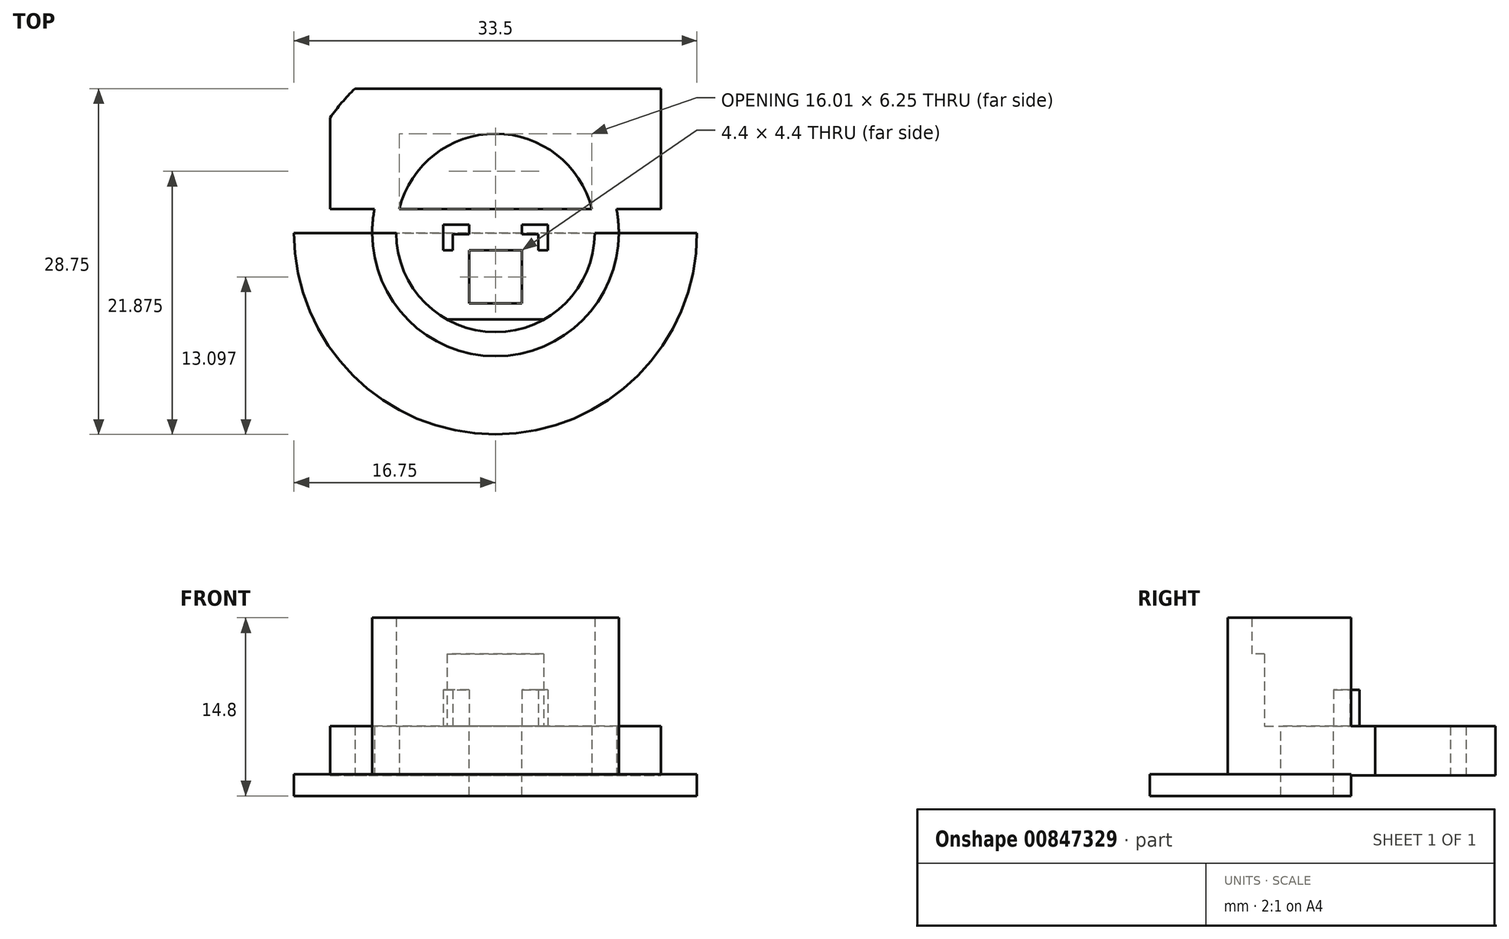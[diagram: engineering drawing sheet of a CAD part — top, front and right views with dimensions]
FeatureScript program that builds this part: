
annotation { "Feature Type Name" : "Feature", "Feature Type Description" : "" }
export const myFeature = defineFeature(function(context is Context, id is Id, definition is map)
    precondition{}
    {
        {
            var Q0;
            Q0=qCreatedBy(makeId("Top.planeOp"),FACE);
            var sketch = newSketch(context, id + "F0", { "sketchPlane" : qUnion([Q0])});
            skCircle(sketch, "E0", {"center": v(0, 0) * mm, "radius": 16.75 * mm});
            skCircle(sketch, "E1", {"center": v(0, 0) * mm, "radius": 10.25 * mm});
            skPoint(sketch, "E2", {"position": v(-16.75, 0) * mm});
            skPoint(sketch, "E3", {"position": v(16.75, 0) * mm});
            skPoint(sketch, "E4", {"position": v(10.25, 0) * mm});
            skPoint(sketch, "E5", {"position": v(-10.25, 0) * mm});
            skLineSegment(sketch, "E6", {"start": v(-16.75, 0) * mm, "end": v(-16.75, 12) * mm});
            skLineSegment(sketch, "E7", {"start": v(-16.75, 12) * mm, "end": v(16.75, 12) * mm});
            skLineSegment(sketch, "E8", {"start": v(16.75, 12) * mm, "end": v(16.75, 0) * mm});
            skLineSegment(sketch, "E9", {"start": v(-16.75, 0) * mm, "end": v(-10.25, 0) * mm});
            skLineSegment(sketch, "E10", {"start": v(10.25, 0) * mm, "end": v(16.75, 0) * mm});
            skLineSegment(sketch, "E11", {"start": v(-10.25, 0) * mm, "end": v(10.25, 0) * mm});
            skLineSegment(sketch, "E12", {"start": v(-13.75, 12) * mm, "end": v(-13.75, 0) * mm});
            skLineSegment(sketch, "E13", {"start": v(13.75, 12) * mm, "end": v(13.75, 0) * mm});
            skCircle(sketch, "E14", {"center": v(0, 0) * mm, "radius": 8.25 * mm});
            skLineSegment(sketch, "E15", {"start": v(-13.75, 2) * mm, "end": v(13.75, 2) * mm});
            skSolve(sketch);
        }
        {
            var Q0;
            {var subQ0=sQuery(id+"F0.wireOp",EDGE,"E9");Q0=makeQuery(id+"F0.imprint","IMPRINT",FACE,{"disambiguationData":[TD([[makeQuery(id+"F0.imprint","IMPRINT",EDGE,{"derivedFrom":subQ0}),-1.0]])]});}
            var Q1;
            {var subQ0=sQuery(id+"F0.wireOp",EDGE,"E11");var subQ4=sQuery(id+"F0.wireOp",EDGE,"E14");var subQ5=makeQuery(id+"F0.imprint","INTERSECT",VERTEX,{"disambiguationData":[OD(0.0)],"derivedFrom":[subQ0,subQ4]});Q1=makeQuery(id+"F0.imprint","IMPRINT",FACE,{"disambiguationData":[TD([[makeQuery(id+"F0.imprint","IMPRINT",EDGE,{"disambiguationData":[TD([[subQ5,-1.0]])],"derivedFrom":subQ4}),-1.0]])]});}
            var Q2;
            {var subQ0=sQuery(id+"F0.wireOp",EDGE,"E14");var subQ1=sQuery(id+"F0.wireOp",EDGE,"E11");var subQ2=makeQuery(id+"F0.imprint","INTERSECT",VERTEX,{"disambiguationData":[OD(0.0)],"derivedFrom":[subQ1,subQ0]});Q2=makeQuery(id+"F0.imprint","IMPRINT",FACE,{"disambiguationData":[TD([[makeQuery(id+"F0.imprint","IMPRINT",EDGE,{"disambiguationData":[TD([[subQ2,-1.0]])],"derivedFrom":subQ1}),-1.0]])]});}
            var Q3;
            {var subQ0=sQuery(id+"F0.wireOp",EDGE,"E11");var subQ4=sQuery(id+"F0.wireOp",EDGE,"E14");var subQ5=makeQuery(id+"F0.imprint","INTERSECT",VERTEX,{"disambiguationData":[OD(0.0)],"derivedFrom":[subQ0,subQ4]});Q3=makeQuery(id+"F0.imprint","IMPRINT",FACE,{"disambiguationData":[TD([[makeQuery(id+"F0.imprint","IMPRINT",EDGE,{"disambiguationData":[TD([[subQ5,-1.0]])],"derivedFrom":subQ4}),-1.0]])]});}
            extrude(context, id + "F1", {"entities" : qUnion([Q0, Q1, Q2, Q3]), "oppositeDirection" : true, "depth" : 1.8 * mm, "offsetDistance" : 25 * mm});
        }
        {
            var Q0;
            {var subQ0=sQuery(id+"F0.wireOp",EDGE,"E13");var subQ1=sQuery(id+"F0.wireOp",EDGE,"E0");var subQ2=makeQuery(id+"F0.imprint","INTERSECT",VERTEX,{"derivedFrom":[subQ1,subQ0]});Q0=makeQuery(id+"F0.imprint","IMPRINT",FACE,{"disambiguationData":[TD([[makeQuery(id+"F0.imprint","IMPRINT",EDGE,{"disambiguationData":[TD([[subQ2,-1.0]])],"derivedFrom":subQ1}),-1.0]])]});}
            var Q1;
            {var subQ0=sQuery(id+"F0.wireOp",EDGE,"E11");Q1=makeQuery(id+"F0.imprint","IMPRINT",FACE,{"disambiguationData":[TD([[makeQuery(id+"F0.imprint","IMPRINT",EDGE,{"derivedFrom":subQ0}),1.0]])]});}
            var Q2;
            {var subQ4=sQuery(id+"F0.wireOp",EDGE,"E13");var subQ10=sQuery(id+"F0.wireOp",EDGE,"E0");var subQ11=makeQuery(id+"F0.imprint","INTERSECT",VERTEX,{"derivedFrom":[subQ10,subQ4]});Q2=makeQuery(id+"F0.imprint","IMPRINT",FACE,{"disambiguationData":[TD([[makeQuery(id+"F0.imprint","IMPRINT",EDGE,{"disambiguationData":[TD([[subQ11,-1.0]])],"derivedFrom":subQ10}),1.0]])]});}
            var Q3;
            {var subQ0=sQuery(id+"F0.wireOp",EDGE,"E14");var subQ1=sQuery(id+"F0.wireOp",EDGE,"E11");var subQ2=makeQuery(id+"F0.imprint","INTERSECT",VERTEX,{"disambiguationData":[OD(0.0)],"derivedFrom":[subQ1,subQ0]});Q3=makeQuery(id+"F0.imprint","IMPRINT",FACE,{"disambiguationData":[TD([[makeQuery(id+"F0.imprint","IMPRINT",EDGE,{"disambiguationData":[TD([[subQ2,-1.0]])],"derivedFrom":subQ1}),1.0]])]});}
            var Q4;
            {var subQ0=sQuery(id+"F0.wireOp",EDGE,"E14");var subQ1=sQuery(id+"F0.wireOp",EDGE,"E11");var subQ2=makeQuery(id+"F0.imprint","INTERSECT",VERTEX,{"disambiguationData":[OD(0.0)],"derivedFrom":[subQ1,subQ0]});Q4=makeQuery(id+"F0.imprint","IMPRINT",FACE,{"disambiguationData":[TD([[makeQuery(id+"F0.imprint","IMPRINT",EDGE,{"disambiguationData":[TD([[subQ2,-1.0]])],"derivedFrom":subQ1}),-1.0]])]});}
            var Q5;
            {var subQ0=sQuery(id+"F0.wireOp",EDGE,"E11");var subQ4=sQuery(id+"F0.wireOp",EDGE,"E14");var subQ5=makeQuery(id+"F0.imprint","INTERSECT",VERTEX,{"disambiguationData":[OD(0.0)],"derivedFrom":[subQ0,subQ4]});Q5=makeQuery(id+"F0.imprint","IMPRINT",FACE,{"disambiguationData":[TD([[makeQuery(id+"F0.imprint","IMPRINT",EDGE,{"disambiguationData":[TD([[subQ5,-1.0]])],"derivedFrom":subQ4}),-1.0]])]});}
            var Q6;
            {var subQ0=sQuery(id+"F0.wireOp",EDGE,"E11");var subQ4=sQuery(id+"F0.wireOp",EDGE,"E14");var subQ5=makeQuery(id+"F0.imprint","INTERSECT",VERTEX,{"disambiguationData":[OD(0.0)],"derivedFrom":[subQ0,subQ4]});Q6=makeQuery(id+"F0.imprint","IMPRINT",FACE,{"disambiguationData":[TD([[makeQuery(id+"F0.imprint","IMPRINT",EDGE,{"disambiguationData":[TD([[subQ5,-1.0]])],"derivedFrom":subQ4}),-1.0]])]});}
            var Q7;
            {var subQ0=sQuery(id+"F0.wireOp",EDGE,"E14");var subQ1=sQuery(id+"F0.wireOp",EDGE,"E11");var subQ2=makeQuery(id+"F0.imprint","INTERSECT",VERTEX,{"disambiguationData":[OD(0.0)],"derivedFrom":[subQ1,subQ0]});Q7=makeQuery(id+"F0.imprint","IMPRINT",FACE,{"disambiguationData":[TD([[makeQuery(id+"F0.imprint","IMPRINT",EDGE,{"disambiguationData":[TD([[subQ2,-1.0]])],"derivedFrom":subQ1}),-1.0]])]});}
            var Q8;
            {var subQ0=sQuery(id+"F0.wireOp",EDGE,"E15");var subQ1=sQuery(id+"F0.wireOp",EDGE,"E1");var subQ2=makeQuery(id+"F0.imprint","INTERSECT",VERTEX,{"disambiguationData":[OD(0.0)],"derivedFrom":[subQ1,subQ0]});Q8=makeQuery(id+"F0.imprint","IMPRINT",FACE,{"disambiguationData":[TD([[makeQuery(id+"F0.imprint","IMPRINT",EDGE,{"disambiguationData":[TD([[subQ2,-1.0]])],"derivedFrom":subQ1}),1.0]])]});}
            var Q9;
            {var subQ0=sQuery(id+"F0.wireOp",EDGE,"E15");var subQ1=sQuery(id+"F0.wireOp",EDGE,"E14");var subQ2=makeQuery(id+"F0.imprint","INTERSECT",VERTEX,{"disambiguationData":[OD(0.0)],"derivedFrom":[subQ1,subQ0]});Q9=makeQuery(id+"F0.imprint","IMPRINT",FACE,{"disambiguationData":[TD([[makeQuery(id+"F0.imprint","IMPRINT",EDGE,{"disambiguationData":[TD([[subQ2,-1.0]])],"derivedFrom":subQ1}),1.0]])]});}
            var Q10;
            {var subQ0=sQuery(id+"F0.wireOp",EDGE,"E7");var subQ1=sQuery(id+"F0.wireOp",EDGE,"E0");var subQ2=makeQuery(id+"F0.imprint","INTERSECT",VERTEX,{"disambiguationData":[OD(1.0)],"derivedFrom":[subQ1,subQ0]});Q10=makeQuery(id+"F0.imprint","IMPRINT",FACE,{"disambiguationData":[TD([[makeQuery(id+"F0.imprint","IMPRINT",EDGE,{"disambiguationData":[TD([[subQ2,-1.0]])],"derivedFrom":subQ1}),-1.0]])]});}
            extrude(context, id + "F2", {"entities" : qUnion([Q0, Q1, Q2, Q3, Q4, Q5, Q6, Q7, Q8, Q9, Q10]), "operationType" : NewBodyOperationType.ADD, "depth" : 4 * mm, "offsetDistance" : 25 * mm, "hasSecondDirection" : true, "secondDirectionOppositeDirection" : true, "secondDirectionDepth" : .1 * mm});
        }
        {
            var Q0;
            {var subQ0=sQuery(id+"F0.wireOp",EDGE,"E11");var subQ4=sQuery(id+"F0.wireOp",EDGE,"E14");var subQ5=makeQuery(id+"F0.imprint","INTERSECT",VERTEX,{"disambiguationData":[OD(0.0)],"derivedFrom":[subQ0,subQ4]});Q0=makeQuery(id+"F0.imprint","IMPRINT",FACE,{"disambiguationData":[TD([[makeQuery(id+"F0.imprint","IMPRINT",EDGE,{"disambiguationData":[TD([[subQ5,-1.0]])],"derivedFrom":subQ4}),-1.0]])]});}
            extrude(context, id + "F3", {"entities" : qUnion([Q0]), "operationType" : NewBodyOperationType.ADD, "depth" : 13 * mm, "offsetDistance" : 25 * mm, "hasSecondDirection" : true, "secondDirectionOppositeDirection" : true, "secondDirectionDepth" : 1.7 * mm});
        }
        {
            var Q0;
            Q0=makeQuery(id+"F2.opExtrude","CAP_FACE",FACE,{"disambiguationData":[OSD([sQuery(id+"F0.wireOp",EDGE,"E1"),sQuery(id+"F0.wireOp",EDGE,"E7"),sQuery(id+"F0.wireOp",EDGE,"E12"),sQuery(id+"F0.wireOp",EDGE,"E13"),sQuery(id+"F0.wireOp",EDGE,"E15")])],"isStart":false});
            var sketch = newSketch(context, id + "F4", { "sketchPlane" : qUnion([Q0])});
            skLineSegment(sketch, "E16.bottom", {"start": v(3.55, -0.1) * mm, "end": v(-3.55, -0.1) * mm});
            skLineSegment(sketch, "E16.top", {"start": v(3.55, -7.2) * mm, "end": v(-3.55, -7.2) * mm});
            skLineSegment(sketch, "E16.left", {"start": v(3.55, -0.1) * mm, "end": v(3.55, -7.2) * mm});
            skLineSegment(sketch, "E16.right", {"start": v(-3.55, -0.1) * mm, "end": v(-3.55, -7.2) * mm});
            skPoint(sketch, "E16.middle", {"position": v(-3.57, -5.17) * mm});
            skPoint(sketch, "E17", {"position": v(-3.55, -3.65) * mm});
            skPoint(sketch, "E18", {"position": v(0, -3.65) * mm});
            skPoint(sketch, "E18.positionSnap0", {"position": v(0, -7.2) * mm});
            skLineSegment(sketch, "E19.bottom", {"start": v(-2.2, -1.45) * mm, "end": v(2.2, -1.45) * mm});
            skLineSegment(sketch, "E19.top", {"start": v(-2.2, -5.85) * mm, "end": v(2.2, -5.85) * mm});
            skLineSegment(sketch, "E19.left", {"start": v(-2.2, -1.45) * mm, "end": v(-2.2, -5.85) * mm});
            skLineSegment(sketch, "E19.right", {"start": v(2.2, -1.45) * mm, "end": v(2.2, -5.85) * mm});
            skLineSegment(sketch, "E20", {"start": v(-3.55, -1.45) * mm, "end": v(-4.35, -1.45) * mm});
            skLineSegment(sketch, "E21", {"start": v(-4.35, -1.45) * mm, "end": v(-4.35, 0.7) * mm});
            skLineSegment(sketch, "E22", {"start": v(-4.35, 0.7) * mm, "end": v(-2.2, 0.7) * mm});
            skLineSegment(sketch, "E23", {"start": v(-2.2, 0.7) * mm, "end": v(-2.2, -0.1) * mm});
            skLineSegment(sketch, "E24", {"start": v(2.2, -0.1) * mm, "end": v(2.2, 0.7) * mm});
            skLineSegment(sketch, "E25", {"start": v(2.2, 0.7) * mm, "end": v(4.35, 0.7) * mm});
            skLineSegment(sketch, "E26", {"start": v(4.35, 0.7) * mm, "end": v(4.35, -1.45) * mm});
            skLineSegment(sketch, "E27", {"start": v(4.35, -1.45) * mm, "end": v(3.55, -1.45) * mm});
            skLineSegment(sketch, "E28", {"start": v(-3.55, -7.2) * mm, "end": v(-4.37, -7.2) * mm});
            skLineSegment(sketch, "E29", {"start": v(-4.37, -7.2) * mm, "end": v(-3.55, -8.43) * mm});
            skLineSegment(sketch, "E30", {"start": v(-3.55, -8.43) * mm, "end": v(3.55, -8.43) * mm});
            skLineSegment(sketch, "E31", {"start": v(3.55, -8.43) * mm, "end": v(4.37, -7.2) * mm});
            skLineSegment(sketch, "E32", {"start": v(4.37, -7.2) * mm, "end": v(3.55, -7.2) * mm});
            skLineSegment(sketch, "E33.bottom", {"start": v(-6, 2.35) * mm, "end": v(6, 2.35) * mm});
            skLineSegment(sketch, "E33.top", {"start": v(-6, -9.65) * mm, "end": v(6, -9.65) * mm});
            skLineSegment(sketch, "E33.left", {"start": v(-6, 2.35) * mm, "end": v(-6, -9.65) * mm});
            skLineSegment(sketch, "E33.right", {"start": v(6, 2.35) * mm, "end": v(6, -9.65) * mm});
            skSolve(sketch);
        }
        {
            var Q0;
            Q0=makeQuery(id+"F4.imprint","IMPRINT",FACE,{"disambiguationData":[TD([[makeQuery(id+"F4.imprint","IMPRINT",EDGE,{"derivedFrom":sQuery(id+"F4.wireOp",EDGE,"E19.bottom")}),-1.0]])]});
            extrude(context, id + "F5", {"entities" : qUnion([Q0]), "operationType" : NewBodyOperationType.REMOVE, "oppositeDirection" : true, "depth" : 10 * mm, "offsetDistance" : 25 * mm});
        }
        {
            var Q0;
            {var subQ4=sQuery(id+"F4.wireOp",EDGE,"E20");Q0=makeQuery(id+"F4.imprint","IMPRINT",FACE,{"disambiguationData":[TD([[makeQuery(id+"F4.imprint","IMPRINT",EDGE,{"derivedFrom":subQ4}),-1.0]])]});}
            var Q1;
            {var subQ0=sQuery(id+"F4.wireOp",EDGE,"E24");Q1=makeQuery(id+"F4.imprint","IMPRINT",FACE,{"disambiguationData":[TD([[makeQuery(id+"F4.imprint","IMPRINT",EDGE,{"derivedFrom":subQ0}),-1.0]])]});}
            extrude(context, id + "F6", {"entities" : qUnion([Q0, Q1]), "operationType" : NewBodyOperationType.ADD, "depth" : 3 * mm, "offsetDistance" : 25 * mm});
        }
        {
            var Q0;
            {var subQ0=sQuery(id+"F4.wireOp",EDGE,"E16.top");Q0=makeQuery(id+"F4.imprint","IMPRINT",FACE,{"disambiguationData":[TD([[makeQuery(id+"F4.imprint","IMPRINT",EDGE,{"derivedFrom":subQ0}),1.0]])]});}
            extrude(context, id + "F7", {"entities" : qUnion([Q0]), "operationType" : NewBodyOperationType.ADD, "depth" : 6 * mm, "offsetDistance" : 25 * mm});
        }
    });
